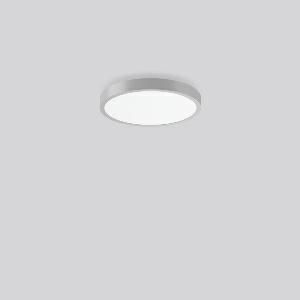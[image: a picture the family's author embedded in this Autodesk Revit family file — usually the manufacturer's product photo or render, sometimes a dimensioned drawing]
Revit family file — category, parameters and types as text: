
# Revit family: triona_round_a_312419_004_2_76_f896
name_source: partatom
category: Lighting Fixtures
units: mm (PartAtom-declared; Revit-internal decimal feet)

## family parameters
Cut with Voids When Loaded = No
Host = Face
Light Source = No
Part Type = Normal
Room Calculation Point = No
Round Connector Dimension = Use Diameter
Shared = No

## types (1)
- TuneableWhite 846 (1 x LED Modul 846, 2450 lm, 4600)
    Apparent Load = 29 VA
    CIE Flux Codes = 48 80 96 100 100
    Color Rendering = 80
    Color Temperature = 4600
    Default Elevation = 1800 mm
    Description = Series: TRIONA round
Decorative round LED surface-mounted luminaire. Flat, seamless frame: aluminium extrusion profile, powder coated. Cover made of sheet steel, powder-coated. Light emission through a diffuser: plastic, opal. Lightguide and diffuser made of non-yellowing plastic (PMMA). Lateral light emission (RZB SIDELITE technology) for above-average homogeneous light distribution. Tunable white versions, dynamically adjustable from 2700 K to 6500 K. Suitable for Ceiling mounting, Wall (surface). Tool-free mounting via bayonet connection. Electronic ballast included. Very easy installation thanks to Plug+Play connection. Ideal for use as part of the Human Centric Lighting concept in connection with RZB light management systems. 
Colour: silver, matt (approx. RAL 9006)
Diameter: 461 mm
Height: 88 mm
Lamp: LED
Socket: without socket
Colour temperature: 2700K - 6500K
Colour rendering index (CRI): 80
System power: 29 W
Rated luminous flux: 2450 lm
Luminous efficiency: 84 lm/W
System power 2: 29 W
Rated luminous flux 2: 2350 lm
Luminous efficiency 2: 81 lm/W
System power 3: 30 W
Rated luminous flux 3: 2400 lm
Luminous efficiency 3: 80 lm/W
Control gear: Converter, dimmable, DALI
Protection class: I
Type of protection: IP 20
    Height = 88 mm
    Lamp = 1 x LED Modul 846
    Lamp Light Flux = 2450 lm
    Lamp count = 1
    Length = 461 mm
    Lifetime = 50000 h
    Luminous efficacy = 84 lm/W
    Manufacturer = RZB
    ModVariant = No
    Model = 312419.004.2.76
    Mounting Place = Ceiling
    Mounting Type = Surface mounted
    Number of Poles = 1
    OnlyDefault = Yes
    Power Factor = 1
    Product Name = TRIONA round A
    Product group = Surface mounted modular luminaires
    ProductGroupID = 306
    Protection Class = Protection class I
    Protection Degree = IP 20
    RLX_Detail_Level = 1
    RLX_Emergency_Light_Flux = 0 lm
    RLX_Emergency_Type = 0
    RLX_Emergency_Type_DB = No
    RlxData = <blob elided: 28621 chars, md5=6cd4efd4>
    Socket = socket
    Standby Power = 0 W
    System Light Flux = 2450 lm
    System Power = 29 W
    Type Comments = TuneableWhite 846
    Type Image = 312420.004.jpg
    URL = http://relux.com
    VarID = tuneablewhite_846
    Voltage = 230 V
    Voltage Range = 220-240 V
    Weight = 0.00 kg
    Width = 0 mm  [stored 0 ft]

note: [stored X ft] marks values corroborated as IEEE doubles in the binary element streams (Revit-internal decimal feet)

## geometry (parser evidence)
native form markers: Blend x4, Sweep x10
no freeform markers — native parametric forms only
